# Revit family: P4908_Double_Adjusting_Conveyor_Nut
name_source: partatom
category: Structural Connections
units: mm (PartAtom-declared; Revit-internal decimal feet)

## family parameters
Always vertical = No
Cut with Voids When Loaded = No
Enable cutting in views = Yes
Material for Model Behavior = Other
Shared = No
Work Plane-Based = Yes

## types (3) — shared parameters
Default Elevation = 48 "
Description = P4908 - Double Adjusting Conveyor Nut
Manufacturer = Atkore Unistrut
Model = P4908
Salsify ID1 = US-P4908
URL = https://www.atkore.com

## per-type parameters (varying)
| type | Material | Power-Strut Part Number | UPC | Weight |
| P4908 HG | Hot Dip Galvanized |  | "786364053806" | 0.18 lbm |
| P4908 EG | Electro Galvanized | PS 3281 3/8 EG | "78636402623" | 0.18 lbm |
| P4908 AL | Aluminum |  | "786364020754" | 0.04 lbm |

note: column(s) folded — value = type name in every type: Part Number

## geometry (parser evidence)
native form markers: Sweep x3
no freeform markers — native parametric forms only
